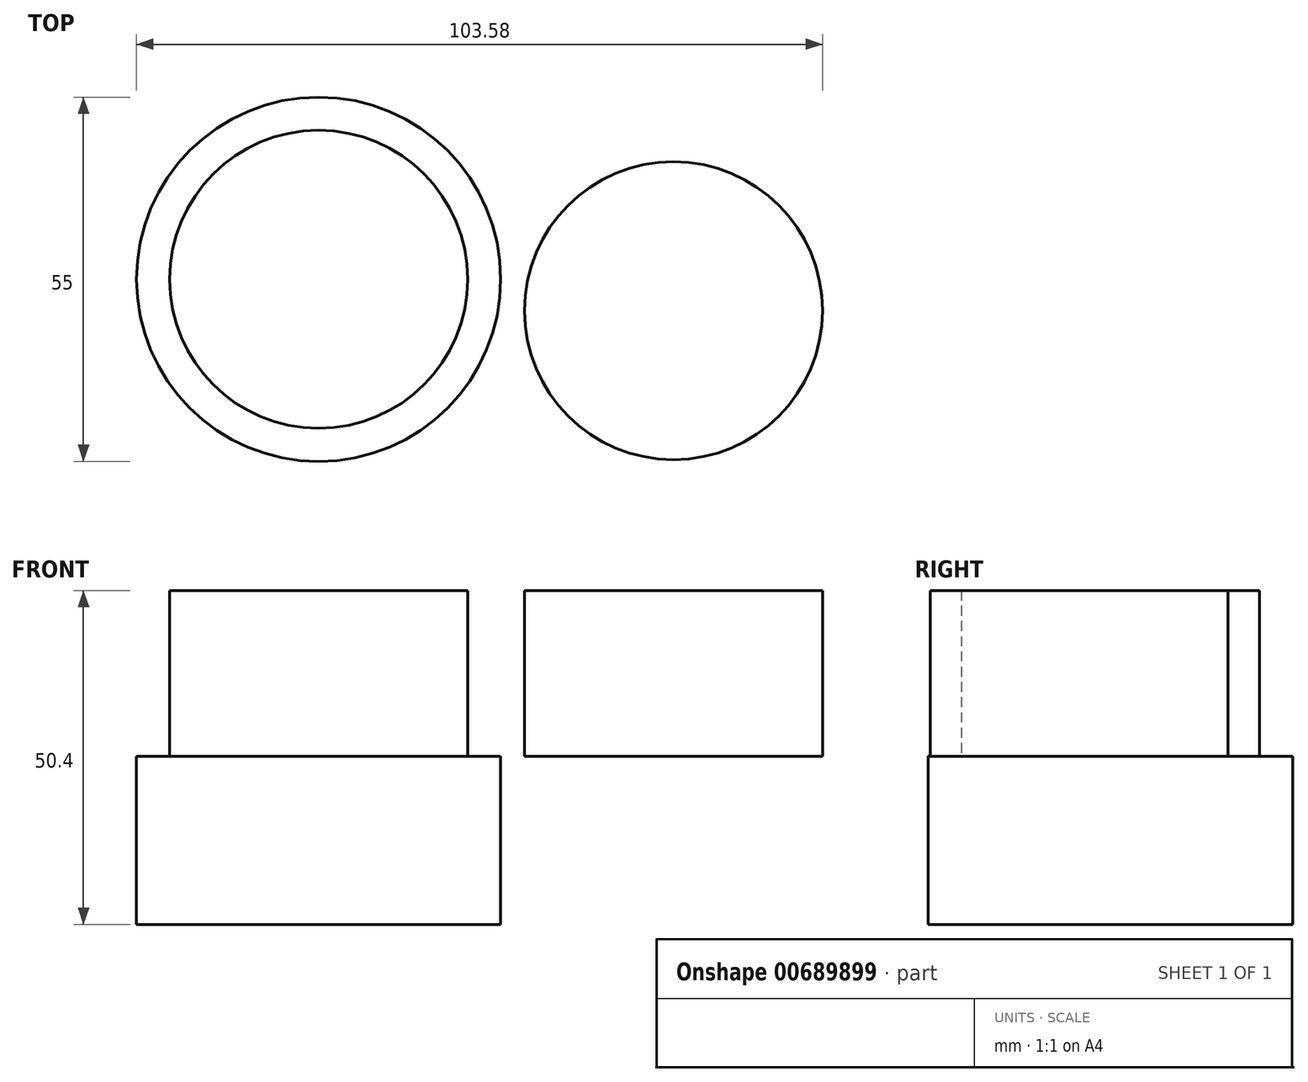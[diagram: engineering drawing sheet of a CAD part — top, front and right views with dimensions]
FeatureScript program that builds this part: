
annotation { "Feature Type Name" : "Feature", "Feature Type Description" : "" }
export const myFeature = defineFeature(function(context is Context, id is Id, definition is map)
    precondition{}
    {
        {
            var Q0;
            Q0=qCreatedBy(makeId("Top.planeOp"),FACE);
            var sketch = newSketch(context, id + "F0", { "sketchPlane" : qUnion([Q0])});
            skCircle(sketch, "E0", {"center": v(28.57, 29.16) * mm, "radius": 27.5 * mm});
            skSolve(sketch);
        }
        {
            var Q0;
            Q0 = qSketchRegion(id + "F0", true);
            extrude(context, id + "F1", {"entities" : qUnion([Q0]), "depth" : 25.4 * mm, "offsetDistance" : 25.4 * mm});
        }
        {
            var Q0;
            Q0=makeQuery(id+"F1.opExtrude","CAP_FACE",FACE,{"disambiguationData":[OSD([sQuery(id+"F0.wireOp",EDGE,"E0")])],"isStart":false});
            var sketch = newSketch(context, id + "F2", { "sketchPlane" : qUnion([Q0])});
            skCircle(sketch, "E1", {"center": v(28.57, 29.16) * mm, "radius": 22.5 * mm});
            skSolve(sketch);
        }
        {
            var Q0;
            Q0 = qSketchRegion(id + "F2", true);
            extrude(context, id + "F3", {"entities" : qUnion([Q0]), "operationType" : NewBodyOperationType.ADD, "depth" : 25 * mm, "offsetDistance" : 25 * mm});
        }
        {
            var Q0;
            Q0=makeQuery(id+"F1.opExtrude","CAP_FACE",FACE,{"disambiguationData":[OSD([sQuery(id+"F0.wireOp",EDGE,"E0")])],"isStart":false});
            var sketch = newSketch(context, id + "F4", { "sketchPlane" : qUnion([Q0])});
            skCircle(sketch, "E2", {"center": v(82.15, 24.42) * mm, "radius": 22.5 * mm});
            skSolve(sketch);
        }
        {
            var Q0;
            Q0 = qSketchRegion(id + "F4", true);
            extrude(context, id + "F5", {"entities" : qUnion([Q0]), "depth" : 25 * mm, "offsetDistance" : 25 * mm});
        }
    });
